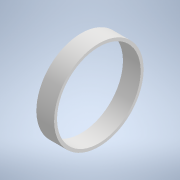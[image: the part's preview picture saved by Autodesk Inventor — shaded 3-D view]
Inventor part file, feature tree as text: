
AUTODESK INVENTOR PART (.ipt)
format: ipt  version: 2020 (Build 240168000, 168)  size: 103,424 bytes
history: native  units: mm
features: extrude x1, sketch x1
ambient origin geometry x8: Origin, YZ Plane, XZ Plane, XY Plane, X Axis, Y Axis, Z Axis, Center Point
bodies: Solid1 (feature_tree)
feature tree (2):
  extrude  "Extrusion1"  Depth=18.0mm
  sketch  "Sketch1"  dims[d0=85.0mm d1=3.0mm d2=18.0mm d3=0.0mm]
